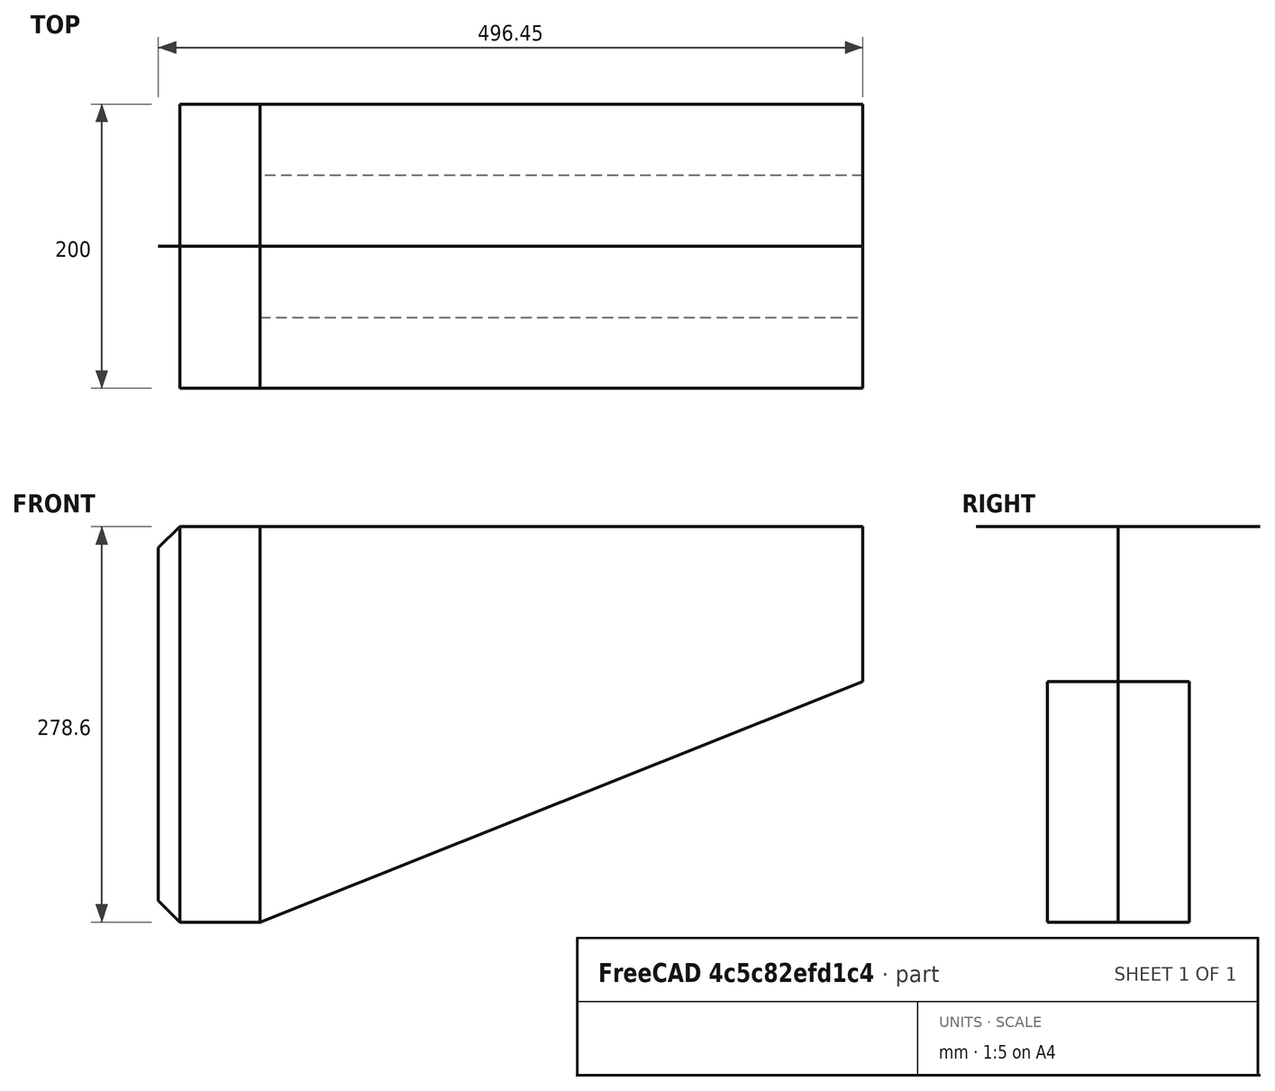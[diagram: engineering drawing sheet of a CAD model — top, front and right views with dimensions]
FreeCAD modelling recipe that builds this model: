
FCSTD DOCUMENT  (FreeCAD 0.21R)
Label: corbel_model
License: Creative Commons Attribution-ShareAlike
LicenseURL: http://creativecommons.org/licenses/by-sa/4.0/
objects: Part::Part2DObjectPython×24, Part::FeaturePython×12, Part::Feature×10, App::DocumentObjectGroup×1
note: 46 computed .brp shape members not serialized (recipe doc carries the construction recipe); baked Part::Feature solids carry a one-line shape summary decoded from their .brp

FEATURE [Part::Feature] Shape
  shape: bbox 2e-07 x 2e-07 x 10 mm, 0 faces, 0 solids (baked)
FEATURE [Part::Feature] Shape001
  shape: bbox 425 x 2e-07 x 2e-07 mm, 0 faces, 0 solids (baked)
FEATURE [Part::Feature] Shape002
  shape: bbox 56.45 x 2e-07 x 2e-07 mm, 0 faces, 0 solids (baked)
FEATURE [Part::Feature] Shape003
  shape: bbox 15 x 2e-07 x 15 mm, 0 faces, 0 solids (baked)
FEATURE [Part::Feature] Shape004
  shape: bbox 2e-07 x 2e-07 x 248.6 mm, 0 faces, 0 solids (baked)
FEATURE [Part::Feature] Shape005
  shape: bbox 15 x 2e-07 x 15 mm, 0 faces, 0 solids (baked)
FEATURE [Part::Feature] Shape006
  shape: bbox 56.45 x 2e-07 x 2e-07 mm, 0 faces, 0 solids (baked)
FEATURE [Part::Feature] Shape007
  shape: bbox 425 x 2e-07 x 169.3 mm, 0 faces, 0 solids (baked)
FEATURE [Part::Feature] Shape008
  shape: bbox 2e-07 x 2e-07 x 109.3 mm, 0 faces, 0 solids (baked)
FEATURE [Part::Part2DObjectPython] Line  # Draft 2D object (typed FeaturePython)
  Area = 0
  ChamferSize = 0
  Closed = false
  End = (496.45,0,169.3)
  FilletRadius = 0
  Length = 50
  MakeFace = true
  Placement = pos=(496.45,-50,169.3) rot=(0,0,1;0rad)
  Points = (2) [(0,0,0),(0,50,0)]
  Start = (496.45,-50,169.3)
  Subdivisions = 0
FEATURE [Part::Part2DObjectPython] Line001  # Draft 2D object (typed FeaturePython)
  Area = 0
  ChamferSize = 0
  Closed = false
  End = (71.45,50,0)
  FilletRadius = 0
  Length = 50
  MakeFace = true
  Placement = pos=(71.45,0,0) rot=(0,0,1;0rad)
  Points = (2) [(0,0,0),(0,50,0)]
  Start = (71.45,0,0)
  Subdivisions = 0
FEATURE [Part::Part2DObjectPython] Line002  # Draft 2D object (typed FeaturePython)
  Area = 0
  ChamferSize = 0
  Closed = false
  End = (71.45,0,0)
  FilletRadius = 0
  Length = 50
  MakeFace = true
  Placement = pos=(71.45,-50,0) rot=(0,0,1;0rad)
  Points = (2) [(0,0,0),(0,50,0)]
  Start = (71.45,-50,0)
  Subdivisions = 0
FEATURE [Part::Part2DObjectPython] Line003  # Draft 2D object (typed FeaturePython)
  Area = 0
  ChamferSize = 0
  Closed = false
  End = (496.45,50,169.3)
  FilletRadius = 0
  Length = 50
  MakeFace = true
  Placement = pos=(496.45,0,169.3) rot=(0,0,1;0rad)
  Points = (2) [(0,0,0),(0,50,0)]
  Start = (496.45,0,169.3)
  Subdivisions = 0
FEATURE [Part::Part2DObjectPython] Line004  # Draft 2D object (typed FeaturePython)
  Area = 0
  ChamferSize = 0
  Closed = false
  End = (71.45,50,0)
  FilletRadius = 0
  Length = 457.479
  MakeFace = true
  Placement = pos=(496.45,50,169.3) rot=(0,0,1;0rad)
  Points = (2) [(0,0,0),(-425,1.42109e-14,-169.3)]
  Start = (496.45,50,169.3)
  Subdivisions = 0
FEATURE [Part::Part2DObjectPython] Line005  # Draft 2D object (typed FeaturePython)
  Area = 0
  ChamferSize = 0
  Closed = false
  End = (71.45,-50,0)
  FilletRadius = 0
  Length = 457.479
  MakeFace = true
  Placement = pos=(496.45,-50,169.3) rot=(0,0,1;0rad)
  Points = (2) [(0,0,0),(-425,1.42109e-14,-169.3)]
  Start = (496.45,-50,169.3)
  Subdivisions = 0
FEATURE [Part::Part2DObjectPython] Line006  # Draft 2D object (typed FeaturePython)
  Area = 0
  ChamferSize = 0
  Closed = false
  End = (496.45,100,278.6)
  FilletRadius = 0
  Length = 100
  MakeFace = true
  Placement = pos=(496.45,0,278.6) rot=(0,0,1;0rad)
  Points = (2) [(0,0,0),(0,100,0)]
  Start = (496.45,0,278.6)
  Subdivisions = 0
FEATURE [Part::Part2DObjectPython] Line007  # Draft 2D object (typed FeaturePython)
  Area = 0
  ChamferSize = 0
  Closed = false
  End = (15,0,278.6)
  FilletRadius = 0
  Length = 100
  MakeFace = true
  Placement = pos=(15,-100,278.6) rot=(0,0,1;0rad)
  Points = (2) [(0,0,0),(0,100,0)]
  Start = (15,-100,278.6)
  Subdivisions = 0
FEATURE [Part::Part2DObjectPython] Line008  # Draft 2D object (typed FeaturePython)
  Area = 0
  ChamferSize = 0
  Closed = false
  End = (15,100,278.6)
  FilletRadius = 0
  Length = 100
  MakeFace = true
  Placement = pos=(15,0,278.6) rot=(0,0,1;0rad)
  Points = (2) [(0,0,0),(0,100,0)]
  Start = (15,0,278.6)
  Subdivisions = 0
FEATURE [Part::Part2DObjectPython] Line009  # Draft 2D object (typed FeaturePython)
  Area = 0
  ChamferSize = 0
  Closed = false
  End = (496.45,0,278.6)
  FilletRadius = 0
  Length = 100
  MakeFace = true
  Placement = pos=(496.45,-100,278.6) rot=(0,0,1;0rad)
  Points = (2) [(0,0,0),(0,100,0)]
  Start = (496.45,-100,278.6)
  Subdivisions = 0
FEATURE [Part::Part2DObjectPython] Line010  # Draft 2D object (typed FeaturePython)
  Area = 0
  ChamferSize = 0
  Closed = false
  End = (15,100,278.6)
  FilletRadius = 0
  Length = 481.45
  MakeFace = true
  Placement = pos=(496.45,100,278.6) rot=(0,0,1;0rad)
  Points = (2) [(0,0,0),(-481.45,1.42109e-14,0)]
  Start = (496.45,100,278.6)
  Subdivisions = 0
FEATURE [Part::Part2DObjectPython] Line011  # Draft 2D object (typed FeaturePython)
  Area = 0
  ChamferSize = 0
  Closed = false
  End = (496.45,-100,278.6)
  FilletRadius = 0
  Length = 481.45
  MakeFace = true
  Placement = pos=(15,-100,278.6) rot=(0,0,1;0rad)
  Points = (2) [(0,0,0),(481.45,-1.42109e-14,0)]
  Start = (15,-100,278.6)
  Subdivisions = 0
FEATURE [Part::Feature] Shape009
  Placement = pos=(0,-100,0) rot=(0,0,1;0rad)
  shape: bbox 425 x 2e-07 x 2e-07 mm, 0 faces, 0 solids (baked)
FEATURE [Part::Part2DObjectPython] Wire006  label="TopFlange"  # Draft 2D object (typed FeaturePython)
  Area = 42500
  ChamferSize = 0
  Closed = true
  End = (71.45,0,278.6)
  FilletRadius = 0
  Length = 1050
  MakeFace = true
  Placement = pos=(71.45,100,278.6) rot=(0,0,1;0rad)
  Points = (4) [(0,0,0),(425,-1.42109e-14,0),(425,-100,0),(0,-100,0)]
  Start = (71.45,100,278.6)
  Subdivisions = 0
FEATURE [Part::Part2DObjectPython] Wire007  label="TopFlange001"  # Draft 2D object (typed FeaturePython)
  Area = 5645
  ChamferSize = 0
  Closed = true
  End = (15,100,278.6)
  FilletRadius = 0
  Length = 312.9
  MakeFace = true
  Placement = pos=(15,0,278.6) rot=(0,0,1;0rad)
  Points = (4) [(0,0,0),(56.45,-1.72828e-15,0),(56.45,100,0),(3.55271e-15,100,0)]
  Start = (15,0,278.6)
  Subdivisions = 0
FEATURE [Part::Part2DObjectPython] Wire008  label="TopFlange002"  # Draft 2D object (typed FeaturePython)
  Area = 5645
  ChamferSize = 0
  Closed = true
  End = (71.45,0,278.6)
  FilletRadius = 0
  Length = 312.9
  MakeFace = true
  Placement = pos=(15,0,278.6) rot=(0,0,1;0rad)
  Points = (4) [(0,0,0),(-3.55271e-15,-100,0),(56.45,-100,0),(56.45,-1.72828e-15,0)]
  Start = (15,0,278.6)
  Subdivisions = 0
FEATURE [Part::Part2DObjectPython] Wire009  label="TopFlange003"  # Draft 2D object (typed FeaturePython)
  Area = 42500
  ChamferSize = 0
  Closed = true
  End = (496.45,0,278.6)
  FilletRadius = 0
  Length = 1050
  MakeFace = true
  Placement = pos=(71.45,0,278.6) rot=(0,0,1;0rad)
  Points = (4) [(0,0,0),(0,-100,0),(425,-100,0),(425,-1.30119e-14,0)]
  Start = (71.45,0,278.6)
  Subdivisions = 0
FEATURE [Part::Part2DObjectPython] Wire010  label="BottomFlange"  # Draft 2D object (typed FeaturePython)
  Area = 22874
  ChamferSize = 0
  Closed = true
  End = (496.45,0,169.3)
  FilletRadius = 0
  Length = 1014.96
  MakeFace = true
  Placement = pos=(71.45,0,0) rot=(0,0,1;0rad)
  Points = (4) [(0,0,0),(-1.42109e-14,-50,0),(425,-50,169.3),(425,-1.30119e-14,169.3)]
  Start = (71.45,0,0)
  Subdivisions = 0
FEATURE [Part::Part2DObjectPython] Wire  label="BottomFlange001"  # Draft 2D object (typed FeaturePython)
  Area = 22874
  ChamferSize = 0
  Closed = true
  End = (71.45,0,0)
  FilletRadius = 0
  Length = 1014.96
  MakeFace = true
  Placement = pos=(496.45,0,169.3) rot=(0,0,1;0rad)
  Points = (4) [(0,0,0),(0,50,0),(-425,50,-169.3),(-425,1.30119e-14,-169.3)]
  Start = (496.45,0,169.3)
  Subdivisions = 0
FEATURE [App::DocumentObjectGroup] Group  label="Aux"
  Group = -> [Shape,Shape001,Shape002,Shape003,Shape004,Shape005,Shape006,Shape007,Shape008,Shape009,Line,Line001,Line002,Line003,Line004,Line005,Line006,Line007,Line008,Line009,Line010,Line011]
FEATURE [Part::Part2DObjectPython] Wire011  label="Web"  # Draft 2D object (typed FeaturePython)
  Area = 82428.8
  ChamferSize = 0
  Closed = true
  End = (71.45,0,278.6)
  FilletRadius = 0
  Length = 1270.38
  MakeFace = true
  Placement = pos=(71.45,0,0) rot=(1,0,0;1.5708rad)
  Points = (4) [(0,0,0),(425,169.3,2.45803e-14),(425,278.6,4.88498e-14),(1.42109e-14,278.6,6.18616e-14)]
  Start = (71.45,0,0)
  Subdivisions = 0
FEATURE [Part::Part2DObjectPython] Wire012  label="Web001"  # Draft 2D object (typed FeaturePython)
  Area = 15727
  ChamferSize = 0
  Closed = true
  End = (15,0,278.6)
  FilletRadius = 0
  Length = 670.1
  MakeFace = true
  Placement = pos=(15,0,0) rot=(1,0,0;1.5708rad)
  Points = (4) [(0,0,0),(56.45,-1.72828e-15,-1.72828e-15),(56.45,278.6,6.01333e-14),(8.88178e-15,278.6,6.18616e-14)]
  Start = (15,0,0)
  Subdivisions = 0
FEATURE [Part::Part2DObjectPython] Wire013  label="Web002"  # Draft 2D object (typed FeaturePython)
  Area = 3954
  ChamferSize = 0
  Closed = true
  End = (15,0,278.6)
  FilletRadius = 0
  Length = 569.626
  MakeFace = true
  Placement = pos=(0,0,263.6) rot=(1,0,0;1.5708rad)
  Points = (4) [(0,0,0),(-7.61118e-15,-248.6,-5.52003e-14),(15,-263.6,-5.89902e-14),(15,15,2.87143e-15)]
  Start = (0,0,263.6)
  Subdivisions = 0
FEATURE [Part::FeaturePython] Component  label="ifcTopFlange"  # Arch/BIM 148 (typed FeaturePython)
  Base = -> Wire006
  HorizontalArea = 0
  IfcData = attributes={"GlobalId": {"name": "GlobalId", "type": "IfcGloballyUniqueId", "is_enum": false, "enum_values": []}, "Description": {"... (+614 chars omitted),+1 more (map truncated)
  IfcType = 148
  MoveBase = false
  MoveWithHost = false
  PerimeterLength = 0
  Placement = pos=(71.45,100,278.6) rot=(0,0,1;0rad)
  PredefinedType = 0
  Thickness = 10
  VerticalArea = 0
FEATURE [Part::FeaturePython] Component001  label="ifcTopFlange001"  # Arch/BIM 148 (typed FeaturePython)
  Base = -> Wire007
  HorizontalArea = 0
  IfcData = attributes={"GlobalId": {"name": "GlobalId", "type": "IfcGloballyUniqueId", "is_enum": false, "enum_values": []}, "Description": {"... (+614 chars omitted),+1 more (map truncated)
  IfcType = 148
  MoveBase = false
  MoveWithHost = false
  PerimeterLength = 0
  Placement = pos=(15,0,278.6) rot=(0,0,1;0rad)
  PredefinedType = 0
  Thickness = 10
  VerticalArea = 0
FEATURE [Part::FeaturePython] Component002  label="ifcTopFlange002"  # Arch/BIM 148 (typed FeaturePython)
  Base = -> Wire008
  HorizontalArea = 0
  IfcData = attributes={"GlobalId": {"name": "GlobalId", "type": "IfcGloballyUniqueId", "is_enum": false, "enum_values": []}, "Description": {"... (+614 chars omitted),+1 more (map truncated)
  IfcType = 148
  MoveBase = false
  MoveWithHost = false
  PerimeterLength = 0
  Placement = pos=(15,0,278.6) rot=(0,0,1;0rad)
  PredefinedType = 0
  Thickness = 10
  VerticalArea = 0
FEATURE [Part::FeaturePython] Component003  label="ifcTopFlange003"  # Arch/BIM 148 (typed FeaturePython)
  Base = -> Wire009
  HorizontalArea = 0
  IfcData = attributes={"GlobalId": {"name": "GlobalId", "type": "IfcGloballyUniqueId", "is_enum": false, "enum_values": []}, "Description": {"... (+614 chars omitted),+1 more (map truncated)
  IfcType = 148
  MoveBase = false
  MoveWithHost = false
  PerimeterLength = 0
  Placement = pos=(71.45,0,278.6) rot=(0,0,1;0rad)
  PredefinedType = 0
  Thickness = 10
  VerticalArea = 0
FEATURE [Part::FeaturePython] Component004  label="ifcWeb"  # Arch/BIM 148 (typed FeaturePython)
  Base = -> Wire011
  HorizontalArea = 0
  IfcData = attributes={"GlobalId": {"name": "GlobalId", "type": "IfcGloballyUniqueId", "is_enum": false, "enum_values": []}, "Description": {"... (+614 chars omitted),+1 more (map truncated)
  IfcType = 148
  MoveBase = false
  MoveWithHost = false
  PerimeterLength = 0
  Placement = pos=(71.45,0,0) rot=(1,0,0;1.5708rad)
  PredefinedType = 0
  Thickness = 10
  VerticalArea = 0
FEATURE [Part::FeaturePython] Component005  label="ifcWeb001"  # Arch/BIM 148 (typed FeaturePython)
  Base = -> Wire012
  HorizontalArea = 0
  IfcData = attributes={"GlobalId": {"name": "GlobalId", "type": "IfcGloballyUniqueId", "is_enum": false, "enum_values": []}, "Description": {"... (+614 chars omitted),+1 more (map truncated)
  IfcType = 148
  MoveBase = false
  MoveWithHost = false
  PerimeterLength = 0
  Placement = pos=(15,0,0) rot=(1,0,0;1.5708rad)
  PredefinedType = 0
  Thickness = 10
  VerticalArea = 0
FEATURE [Part::FeaturePython] Component006  label="ifcWeb002"  # Arch/BIM 148 (typed FeaturePython)
  Base = -> Wire013
  HorizontalArea = 0
  IfcData = attributes={"GlobalId": {"name": "GlobalId", "type": "IfcGloballyUniqueId", "is_enum": false, "enum_values": []}, "Description": {"... (+614 chars omitted),+1 more (map truncated)
  IfcType = 148
  MoveBase = false
  MoveWithHost = false
  PerimeterLength = 0
  Placement = pos=(0,0,263.6) rot=(1,0,0;1.5708rad)
  PredefinedType = 0
  Thickness = 10
  VerticalArea = 0
FEATURE [Part::FeaturePython] Component007  label="ifcBottomFlange"  # Arch/BIM 148 (typed FeaturePython)
  Base = -> Wire010
  HorizontalArea = 0
  IfcData = attributes={"GlobalId": {"name": "GlobalId", "type": "IfcGloballyUniqueId", "is_enum": false, "enum_values": []}, "Description": {"... (+614 chars omitted),+1 more (map truncated)
  IfcType = 148
  MoveBase = false
  MoveWithHost = false
  PerimeterLength = 0
  Placement = pos=(71.45,0,0) rot=(0,0,1;0rad)
  PredefinedType = 0
  Thickness = 10
  VerticalArea = 0
FEATURE [Part::FeaturePython] Component008  label="ifcBottomFlange001"  # Arch/BIM 148 (typed FeaturePython)
  Base = -> Wire
  HorizontalArea = 0
  IfcData = attributes={"GlobalId": {"name": "GlobalId", "type": "IfcGloballyUniqueId", "is_enum": false, "enum_values": []}, "Description": {"... (+614 chars omitted),+1 more (map truncated)
  IfcType = 148
  MoveBase = false
  MoveWithHost = false
  PerimeterLength = 0
  Placement = pos=(496.45,0,169.3) rot=(0,0,1;0rad)
  PredefinedType = 0
  Thickness = 10
  VerticalArea = 0
FEATURE [Part::Part2DObjectPython] Line012  # Draft 2D object (typed FeaturePython)
  Area = 0
  ChamferSize = 0
  Closed = false
  End = (15,100,278.6)
  FilletRadius = 0
  Length = 200
  MakeFace = true
  Placement = pos=(15,-100,278.6) rot=(1,0,0;1.5708rad)
  Points = (2) [(0,0,0),(-1.24345e-14,-1.7053e-13,-200)]
  Start = (15,-100,278.6)
  Subdivisions = 0
FEATURE [Part::Part2DObjectPython] Line013  # Draft 2D object (typed FeaturePython)
  Area = 0
  ChamferSize = 0
  Closed = false
  End = (0,0,15)
  FilletRadius = 0
  Length = 248.6
  MakeFace = true
  Placement = pos=(0,0,263.6) rot=(1,0,0;1.5708rad)
  Points = (2) [(0,0,0),(-7.61118e-15,-248.6,-5.52003e-14)]
  Start = (0,0,263.6)
  Subdivisions = 0
FEATURE [Part::Part2DObjectPython] Line014  # Draft 2D object (typed FeaturePython)
  Area = 0
  ChamferSize = 0
  Closed = false
  End = (15,0,0)
  FilletRadius = 0
  Length = 56.45
  MakeFace = true
  Placement = pos=(71.45,0,0) rot=(1,0,0;1.5708rad)
  Points = (2) [(0,0,0),(-56.45,1.72828e-15,1.72828e-15)]
  Start = (71.45,0,0)
  Subdivisions = 0
FEATURE [Part::FeaturePython] Component009  label="ifcWelds"  # Arch/BIM 137 (typed FeaturePython)
  Base = -> Line012
  GlobalOrLocal = 0
  HorizontalArea = 0
  IfcData = attributes={"GlobalId": {"name": "GlobalId", "type": "IfcGloballyUniqueId", "is_enum": false, "enum_values": []}, "Description": {"... (+681 chars omitted),+1 more (map truncated)
  IfcType = 137
  MoveBase = false
  MoveWithHost = false
  PerimeterLength = 0
  Placement = pos=(15,-100,278.6) rot=(1,0,0;1.5708rad)
  PredefinedType = 0
  VerticalArea = 0
FEATURE [Part::FeaturePython] Component010  label="ifcWelds001"  # Arch/BIM 137 (typed FeaturePython)
  Base = -> Line013
  GlobalOrLocal = 0
  HorizontalArea = 0
  IfcData = attributes={"GlobalId": {"name": "GlobalId", "type": "IfcGloballyUniqueId", "is_enum": false, "enum_values": []}, "Description": {"... (+681 chars omitted),+1 more (map truncated)
  IfcType = 137
  MoveBase = false
  MoveWithHost = false
  PerimeterLength = 0
  Placement = pos=(0,0,263.6) rot=(1,0,0;1.5708rad)
  PredefinedType = 0
  VerticalArea = 0
FEATURE [Part::FeaturePython] Component011  label="ifcWelds002"  # Arch/BIM 137 (typed FeaturePython)
  Base = -> Line014
  GlobalOrLocal = 0
  HorizontalArea = 0
  IfcData = attributes={"GlobalId": {"name": "GlobalId", "type": "IfcGloballyUniqueId", "is_enum": false, "enum_values": []}, "Description": {"... (+681 chars omitted),+1 more (map truncated)
  IfcType = 137
  MoveBase = false
  MoveWithHost = false
  PerimeterLength = 0
  Placement = pos=(71.45,0,0) rot=(1,0,0;1.5708rad)
  PredefinedType = 0
  VerticalArea = 0
